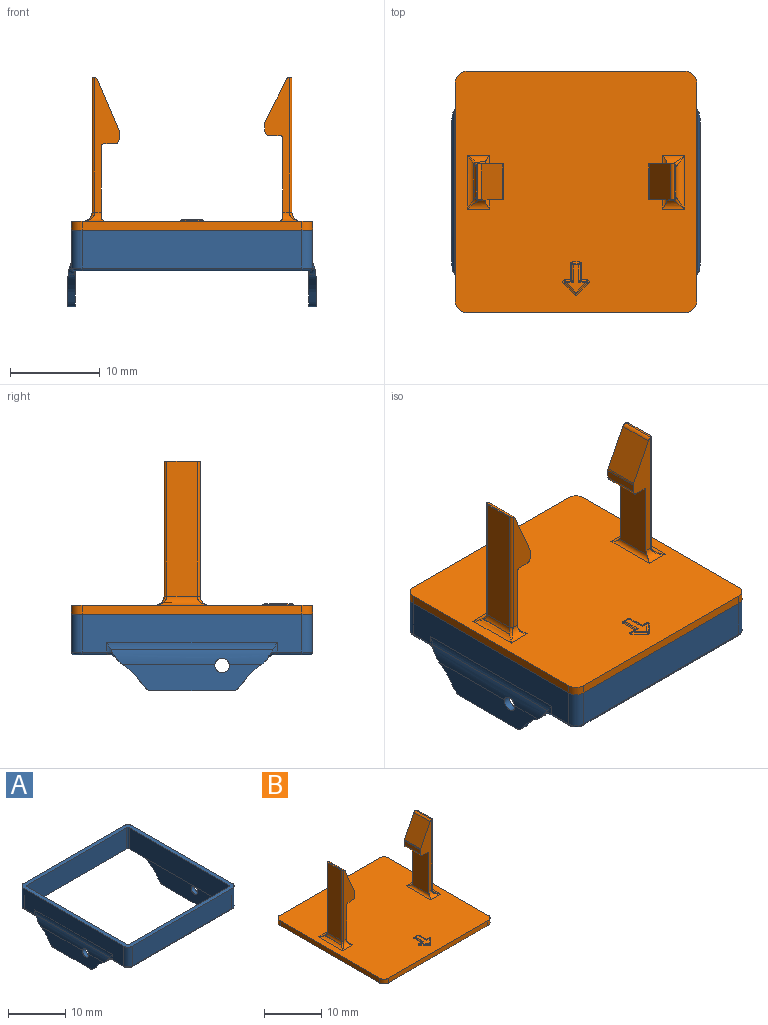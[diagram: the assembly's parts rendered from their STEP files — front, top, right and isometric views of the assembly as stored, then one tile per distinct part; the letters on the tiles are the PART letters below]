
ASSEMBLY  parts=2 mates=1
PART A: 56 faces, bbox 28.8x27x8.5 mm
  f0: plane 15.73x3.06mm, normal (1,0,0), area 35mm2, adj f2,f21,f22,f23,f54
  f1: cylinder r=5mm len=18mm, axis (0,1,0), area 26.9mm2, adj f25,f26,f28,f30,f42,f43,f51,f52
  f2: cylinder r=5mm len=18mm, axis (0,1,0), area 26.9mm2, adj f0,f21,f23,f31,f45,f46,f48,f49
  f3: plane 26.2x26.2mm, normal (0,0,-1), area 47.2mm2, adj f11,f12,f13,f14,f15,f16,f17,f18
  f4: plane 24.4x4.2mm, normal (0,-1,0), area 102.5mm2, adj f5,f19,f20,f39
  f5: cylinder r=1.2mm len=4.2mm, axis (0,0,-1), area 7.9mm2, adj f4,f6,f20,f40
  f6: plane 24.4x4.2mm, normal (1,0,0), area 82.4mm2, adj f5,f7,f20,f31,f36,f41,f45,f48
  f7: cylinder r=1.2mm len=4.2mm, axis (0,0,-1), area 7.9mm2, adj f6,f8,f20,f35
  f8: plane 24.4x4.2mm, normal (0,1,0), area 102.5mm2, adj f7,f9,f20,f34
  f9: cylinder r=1.2mm len=4.2mm, axis (0,0,-1), area 7.9mm2, adj f8,f10,f20,f33
  f10: plane 24.4x4.2mm, normal (-1,0,0), area 82.4mm2, adj f9,f19,f20,f30,f32,f37,f42,f51
  f11: plane 24.4x4.5mm, normal (0,-1,0), area 109.8mm2, adj f3,f12,f18,f20
  f12: cylinder r=0.4mm len=4.5mm, axis (0,0,-1), area 2.8mm2, adj f3,f11,f13,f20
  f13: plane 24.4x4.5mm, normal (-1,0,0), area 109.8mm2, adj f3,f12,f14,f20
  f14: cylinder r=0.4mm len=4.5mm, axis (0,0,-1), area 2.8mm2, adj f3,f13,f15,f20
  f15: plane 24.4x4.5mm, normal (0,1,0), area 109.8mm2, adj f3,f14,f16,f20
  f16: cylinder r=0.4mm len=4.5mm, axis (0,0,-1), area 2.8mm2, adj f3,f15,f17,f20
  f17: plane 24.4x4.5mm, normal (1,0,0), area 109.8mm2, adj f3,f16,f18,f20
  f18: cylinder r=0.4mm len=4.5mm, axis (0,0,-1), area 2.8mm2, adj f3,f11,f17,f20
  f19: cylinder r=1.2mm len=4.2mm, axis (0,0,-1), area 7.9mm2, adj f4,f10,f20,f38
  f20: plane 26.8x26.8mm, normal (0,0,1), area 82.1mm2, adj f4,f5,f6,f7,f8,f9,f10,f11
  f21: extruded ~3.91x3.63mm, area 4.3mm2, adj f0,f2,f22,f24,f46,f47
  f22: plane 9x0.8mm, normal (0,0,-1), area 7.2mm2, adj f0,f21,f23,f24
  f23: extruded ~3.91x3.63mm, area 4.3mm2, adj f0,f2,f22,f24,f49,f50
  f24: plane 18.4x4mm, normal (-1,0,0), area 51.8mm2, adj f3,f21,f22,f23,f47,f50,f54
  f25: extruded ~3.91x3.63mm, area 4.3mm2, adj f1,f27,f28,f29,f52,f53
  f26: extruded ~3.91x3.63mm, area 4.3mm2, adj f1,f27,f28,f29,f43,f44
  f27: plane 9x0.8mm, normal (0,0,-1), area 7.2mm2, adj f25,f26,f28,f29
  f28: plane 15.73x3.06mm, normal (-1,0,0), area 35mm2, adj f1,f25,f26,f27,f55
  f29: plane 18.4x4mm, normal (1,0,0), area 51.8mm2, adj f3,f25,f26,f27,f44,f53,f55
  f30: cylinder r=2.5mm len=19mm, axis (0,1,0), area 15.2mm2, adj f1,f10,f42,f51
  f31: cylinder r=2.5mm len=19mm, axis (0,1,0), area 15.2mm2, adj f2,f6,f45,f48
  f32: cylinder r=0.3mm len=3mm, axis (0,-1,0), area 1.3mm2, adj f3,f10,f33,f43
  f33: torus R=0.9mm, axis (0,0,1), area 0.8mm2, adj f3,f9,f32,f34
  f34: cylinder r=0.3mm len=24.4mm, axis (-1,0,0), area 11.5mm2, adj f3,f8,f33,f35
  f35: torus R=0.9mm, axis (0,0,1), area 0.8mm2, adj f3,f7,f34,f36
  f36: cylinder r=0.3mm len=3mm, axis (0,1,0), area 1.3mm2, adj f3,f6,f35,f49
  f37: cylinder r=0.3mm len=3mm, axis (0,-1,0), area 1.3mm2, adj f3,f10,f38,f52
  f38: torus R=0.9mm, axis (0,0,1), area 0.8mm2, adj f3,f19,f37,f39
  f39: cylinder r=0.3mm len=24.4mm, axis (1,0,0), area 11.5mm2, adj f3,f4,f38,f40
  f40: torus R=0.9mm, axis (0,0,1), area 0.8mm2, adj f3,f5,f39,f41
  f41: cylinder r=0.3mm len=3mm, axis (0,1,0), area 1.3mm2, adj f3,f6,f40,f46
  f42: bspline ~2.14x1mm, area 0.4mm2, adj f1,f10,f30,f43
  f43: bspline ~1.57x1.14mm, area 0.9mm2, adj f1,f26,f32,f42,f44
  f44: cylinder r=1mm len=0.84mm, axis (1,0,0), area 0.1mm2, adj f3,f26,f29,f43
  f45: bspline ~2.14x1mm, area 0.4mm2, adj f2,f6,f31,f46
  f46: bspline ~1.57x1.14mm, area 0.9mm2, adj f2,f21,f41,f45,f47
  f47: cylinder r=1mm len=0.84mm, axis (-1,0,0), area 0.1mm2, adj f3,f21,f24,f46
  f48: bspline ~2.14x1mm, area 0.4mm2, adj f2,f6,f31,f49
  f49: bspline ~1.57x1.14mm, area 0.9mm2, adj f2,f23,f36,f48,f50
  f50: cylinder r=1mm len=0.84mm, axis (-1,0,0), area 0.1mm2, adj f3,f23,f24,f49
  f51: bspline ~2.14x1mm, area 0.4mm2, adj f1,f10,f30,f52
  f52: bspline ~1.57x1.14mm, area 0.9mm2, adj f1,f25,f37,f51,f53
  f53: cylinder r=1mm len=0.84mm, axis (1,0,0), area 0.1mm2, adj f3,f25,f29,f52
  f54: cylinder r=0.81mm len=1.62mm, axis (1,0,0), area 4.1mm2, adj f0,f2,f24
  f55: cylinder r=0.81mm len=1.62mm, axis (1,0,0), area 4.1mm2, adj f1,f28,f29
PART B: 79 faces, bbox 26.8x26.8x17 mm
  f0: plane 14.99x2.7mm, normal (0,1,0), area 17.2mm2, adj f7,f8,f9,f10,f21,f22,f23,f27
  f1: plane 14.98x2.7mm, normal (0,-1,0), area 17.9mm2, adj f12,f13,f14,f15,f24,f25,f26,f28
  f2: plane 14.99x2.7mm, normal (0,-1,0), area 17.2mm2, adj f7,f8,f9,f10,f21,f22,f23,f27
  f3: plane 15x3.4mm, normal (-1,0,0), area 51mm2, adj f16,f60,f70,f72
  f4: plane 26.8x26.8mm, normal (0,0,-1), area 717mm2, adj f18,f19,f20,f58,f75,f76,f77,f78
  f5: plane 15x3.4mm, normal (1,0,0), area 51mm2, adj f6,f63,f66,f68
  f6: plane 3.96x0.19mm, normal (0,0,1), area 0.7mm2, adj f5,f21,f66,f68
  f7: plane 4.62x4mm, normal (-0.89,0,0.45), area 20.7mm2, adj f0,f2,f21,f22
  f8: plane 4x0.88mm, normal (-1,0,0), area 3.5mm2, adj f0,f2,f22,f23
  f9: plane 4x1.2mm, normal (0,0,-1), area 4.8mm2, adj f0,f2,f23,f27
  f10: plane 8.7x4.27mm, normal (-1,0,0), area 34.8mm2, adj f0,f2,f27,f62,f64,f73
  f11: plane 26.8x26.8mm, normal (0,0,1), area 681.5mm2, adj f18,f19,f20,f44,f45,f47,f48,f49
  f12: plane 7.8x4.27mm, normal (1,0,0), area 31.2mm2, adj f1,f17,f28,f59,f61,f74
  f13: plane 4x1.2mm, normal (0,0,-1), area 4.8mm2, adj f1,f17,f24,f28
  f14: plane 4x0.9mm, normal (1,0,0), area 3.6mm2, adj f1,f17,f24,f25
  f15: plane 5.5x4mm, normal (0.92,0,0.39), area 23.9mm2, adj f1,f17,f25,f26
  f16: plane 3.94x0.17mm, normal (0,0,1), area 0.6mm2, adj f3,f26,f70,f72
  f17: plane 14.98x2.7mm, normal (0,1,0), area 17.9mm2, adj f12,f13,f14,f15,f24,f25,f26,f28
  f18: plane 24.4x1mm, normal (-1,0,0), area 24.4mm2, adj f4,f11,f76,f77
  f19: plane 24.4x1mm, normal (1,0,0), area 24.4mm2, adj f4,f11,f75,f78
  f20: plane 24.4x1mm, normal (0,-1,0), area 24.4mm2, adj f4,f11,f77,f78
  f21: cylinder r=0.5mm len=4mm, axis (0,1,0), area 2.2mm2, adj f0,f2,f6,f7,f66,f68
  f22: cylinder r=0.5mm len=4mm, axis (0,1,0), area 0.9mm2, adj f0,f2,f7,f8
  f23: cylinder r=0.5mm len=4mm, axis (0,1,0), area 3.1mm2, adj f0,f2,f8,f9
  f24: cylinder r=0.5mm len=4mm, axis (0,1,0), area 3.1mm2, adj f1,f13,f14,f17
  f25: cylinder r=0.5mm len=4mm, axis (0,1,0), area 0.8mm2, adj f1,f14,f15,f17
  f26: cylinder r=0.5mm len=4mm, axis (0,1,0), area 2.3mm2, adj f1,f15,f16,f17,f70,f72
  f27: cylinder r=0.3mm len=4mm, axis (0,-1,0), area 1.9mm2, adj f0,f2,f9,f10
  f28: cylinder r=0.3mm len=4mm, axis (0,-1,0), area 1.9mm2, adj f1,f12,f13,f17
  f29: plane 3.03x2.07mm, normal (0,0,1), area 2.3mm2, adj f30,f31,f32,f33,f34,f35,f36
  f30: cylinder r=0.2mm len=1.33mm, axis (0.71,0.71,0), area 0.3mm2, adj f29,f37,f38,f56
  f31: cylinder r=0.2mm len=0.91mm, axis (-1,0,0), area 0.1mm2, adj f29,f37,f39,f55
  f32: cylinder r=0.2mm len=1.33mm, axis (-0.71,0.71,0), area 0.3mm2, adj f29,f38,f40,f52
  f33: cylinder r=0.2mm len=2.08mm, axis (0,1,0), area 0.3mm2, adj f29,f39,f41,f51
  f34: cylinder r=0.2mm len=0.91mm, axis (1,0,0), area 0.1mm2, adj f29,f40,f42,f48
  f35: cylinder r=0.2mm len=0.77mm, axis (-1,0,0), area 0.1mm2, adj f29,f41,f43,f47
  f36: cylinder r=0.2mm len=2.08mm, axis (0,1,0), area 0.3mm2, adj f29,f42,f43,f44
  f37: bspline ~0.28x0.17mm, area 0mm2, adj f30,f31,f57
  f38: bspline ~0.21x0.12mm, area 0mm2, adj f30,f32,f54
  f39: bspline ~0.26x0.26mm, area 0mm2, adj f31,f33,f53
  f40: bspline ~0.28x0.17mm, area 0mm2, adj f32,f34,f50
  f41: bspline ~0.17x0.17mm, area 0mm2, adj f33,f35,f49
  f42: bspline ~0.26x0.26mm, area 0mm2, adj f34,f36,f46
  f43: bspline ~0.17x0.17mm, area 0mm2, adj f35,f36,f45
  f44: cylinder r=0.2mm len=1.84mm, axis (0,1,0), area 0.3mm2, adj f11,f36,f45,f46
  f45: bspline ~0.3x0.25mm, area 0mm2, adj f11,f43,f44,f47
  f46: bspline ~0.17x0.17mm, area 0mm2, adj f42,f44,f48
  f47: cylinder r=0.2mm len=0.77mm, axis (-1,0,0), area 0.1mm2, adj f11,f35,f45,f49
  f48: cylinder r=0.2mm len=0.68mm, axis (1,0,0), area 0.1mm2, adj f11,f34,f46,f50
  f49: bspline ~0.3x0.25mm, area 0mm2, adj f11,f41,f47,f51
  f50: bspline ~0.42x0.37mm, area 0.1mm2, adj f11,f40,f48,f52
  f51: cylinder r=0.2mm len=1.84mm, axis (0,1,0), area 0.3mm2, adj f11,f33,f49,f53
  f52: cylinder r=0.2mm len=1.33mm, axis (-0.71,0.71,0), area 0.3mm2, adj f11,f32,f50,f54
  f53: bspline ~0.17x0.17mm, area 0mm2, adj f39,f51,f55
  f54: bspline ~0.39x0.21mm, area 0mm2, adj f11,f38,f52,f56
  f55: cylinder r=0.2mm len=0.68mm, axis (-1,0,0), area 0.1mm2, adj f11,f31,f53,f57
  f56: cylinder r=0.2mm len=1.33mm, axis (0.71,0.71,0), area 0.3mm2, adj f11,f30,f54,f57
  f57: bspline ~0.48x0.28mm, area 0.1mm2, adj f11,f37,f55,f56
  f58: plane 24.4x1mm, normal (0,1,0), area 24.4mm2, adj f4,f11,f75,f76
  f59: cylinder r=1mm len=2.5mm, axis (-1,0,0), area 2.1mm2, adj f1,f11,f12,f69,f74
  f60: cylinder r=1mm len=6mm, axis (0,1,0), area 7.4mm2, adj f3,f11,f69,f71
  f61: cylinder r=1mm len=2.5mm, axis (-1,0,0), area 2.1mm2, adj f11,f12,f17,f71,f74
  f62: cylinder r=1mm len=2.5mm, axis (-1,0,0), area 2.1mm2, adj f2,f10,f11,f65,f73
  f63: cylinder r=1mm len=6mm, axis (0,-1,0), area 7.4mm2, adj f5,f11,f65,f67
  f64: cylinder r=1mm len=2.5mm, axis (-1,0,0), area 2.1mm2, adj f0,f10,f11,f67,f73
  f65: bspline ~1.3x1.3mm, area 0.3mm2, adj f62,f63,f66
  f66: cylinder r=0.3mm len=15mm, axis (0,0,-1), area 7.1mm2, adj f2,f5,f6,f21,f65
  f67: bspline ~1.3x1.3mm, area 0.3mm2, adj f63,f64,f68
  f68: cylinder r=0.3mm len=15mm, axis (0,0,1), area 7.1mm2, adj f0,f5,f6,f21,f67
  f69: bspline ~1.3x1.3mm, area 0.3mm2, adj f59,f60,f70
  f70: cylinder r=0.3mm len=15mm, axis (0,0,1), area 7.1mm2, adj f1,f3,f16,f26,f69
  f71: bspline ~1.3x1.3mm, area 0.3mm2, adj f60,f61,f72
  f72: cylinder r=0.3mm len=15mm, axis (0,0,-1), area 7.1mm2, adj f3,f16,f17,f26,f71
  f73: cylinder r=0.5mm len=6mm, axis (0,-1,0), area 4mm2, adj f10,f11,f62,f64
  f74: cylinder r=0.5mm len=6mm, axis (0,1,0), area 4mm2, adj f11,f12,f59,f61
  f75: cylinder r=1.2mm len=1.2mm, axis (0,0,-1), area 1.9mm2, adj f4,f11,f19,f58
  f76: cylinder r=1.2mm len=1.2mm, axis (0,0,1), area 1.9mm2, adj f4,f11,f18,f58
  f77: cylinder r=1.2mm len=1.2mm, axis (0,0,1), area 1.9mm2, adj f4,f11,f18,f20
  f78: cylinder r=1.2mm len=1.2mm, axis (0,0,-1), area 1.9mm2, adj f4,f11,f19,f20
PLACE A at identity fixed
PLACE B t=(0,3.1,5.5)mm
MATE fastened B.f4 <-> A.f20  axis (0,0,-1) through (0,0,4.5)mm
